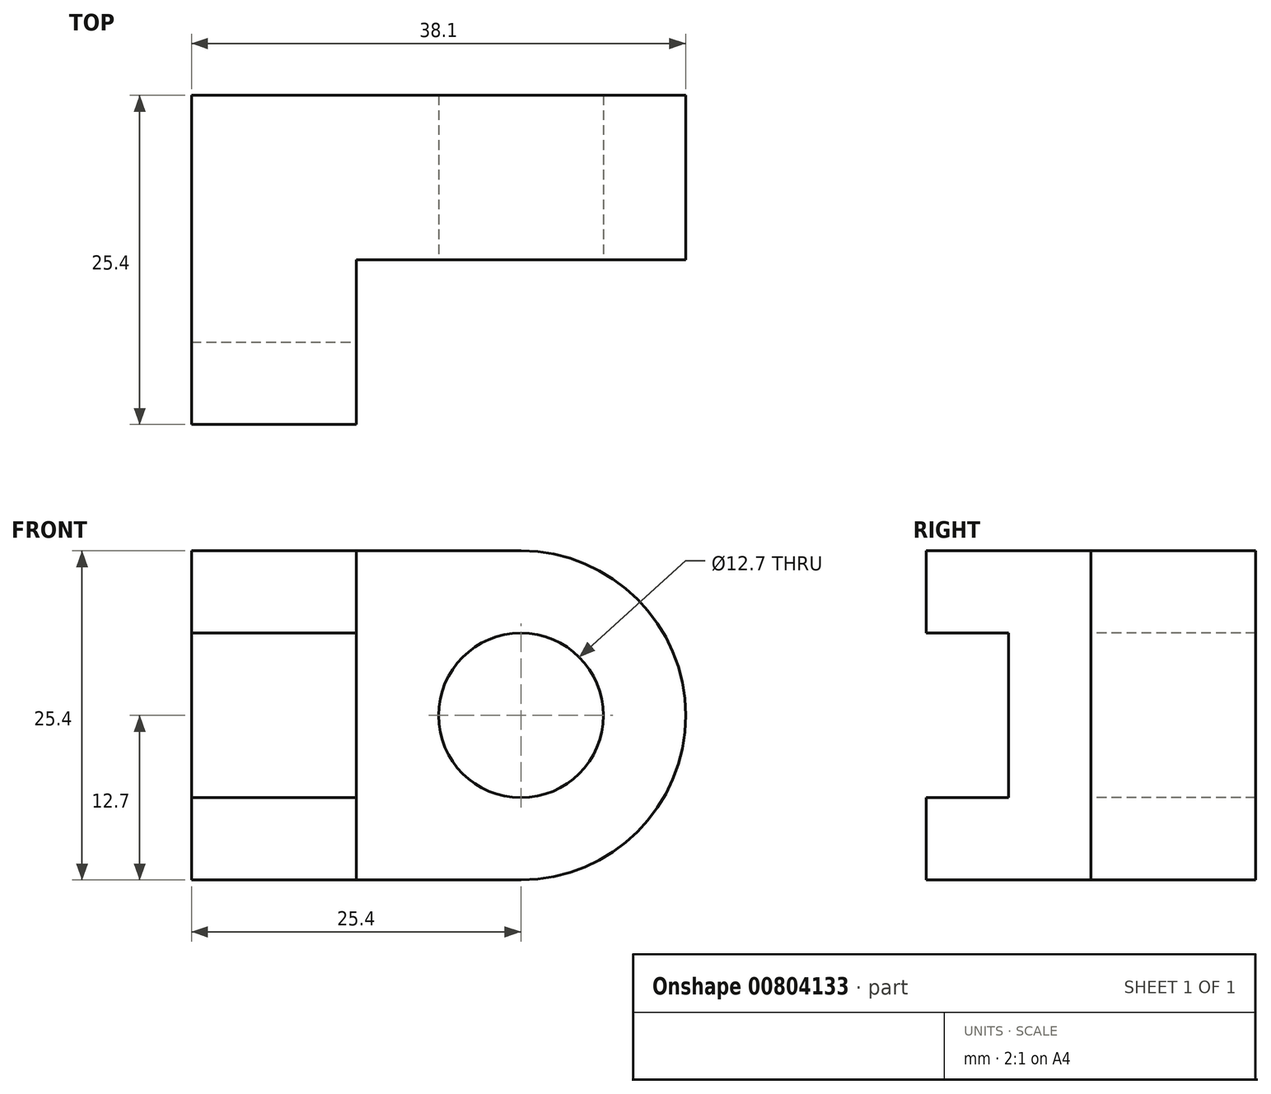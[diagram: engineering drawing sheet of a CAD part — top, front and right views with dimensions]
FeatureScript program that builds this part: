
annotation { "Feature Type Name" : "Feature", "Feature Type Description" : "" }
export const myFeature = defineFeature(function(context is Context, id is Id, definition is map)
    precondition{}
    {
        {
            var Q0;
            Q0=qCreatedBy(makeId("Front.planeOp"),FACE);
            var sketch = newSketch(context, id + "F0", { "sketchPlane" : qUnion([Q0])});
            skLineSegment(sketch, "E0", {"start": v(0, 0) * mm, "end": v(0, 25.4) * mm});
            skLineSegment(sketch, "E1", {"start": v(0, 25.4) * mm, "end": v(31.75, 25.4) * mm});
            skLineSegment(sketch, "E2", {"start": v(31.75, 25.4) * mm, "end": v(31.75, 0) * mm});
            skLineSegment(sketch, "E3", {"start": v(31.75, 0) * mm, "end": v(0, 0) * mm});
            skSolve(sketch);
        }
        {
            var Q0;
            Q0=makeQuery(id+"F0.imprint","IMPRINT",FACE,{"disambiguationData":[TD([[makeQuery(id+"F0.imprint","IMPRINT",EDGE,{"derivedFrom":sQuery(id+"F0.wireOp",EDGE,"E0")}),-1.0]])]});
            extrude(context, id + "F1", {"entities" : qUnion([Q0]), "depth" : 25.4 * mm, "offsetDistance" : 25.4 * mm});
        }
        {
            var Q0;
            Q0=makeQuery(id+"F1.opExtrude","SWEPT_FACE",FACE,{"disambiguationData":[OSD([sQuery(id+"F0.wireOp",EDGE,"E2")])]});
            var sketch = newSketch(context, id + "F2", { "sketchPlane" : qUnion([Q0])});
            skLineSegment(sketch, "E4", {"start": v(-25.4, 0) * mm, "end": v(-12.7, 0) * mm});
            skLineSegment(sketch, "E5", {"start": v(-12.7, 0) * mm, "end": v(-12.7, 25.4) * mm});
            skSolve(sketch);
        }
        {
            var Q0;
            Q0=makeQuery(id+"F2.imprint","IMPRINT",FACE,{"disambiguationData":[TD([[makeQuery(id+"F2.imprint","IMPRINT",EDGE,{"derivedFrom":sQuery(id+"F2.wireOp",EDGE,"E4")}),1.0]])]});
            extrude(context, id + "F3", {"entities" : qUnion([Q0]), "operationType" : NewBodyOperationType.REMOVE, "oppositeDirection" : true, "depth" : 19.05 * mm, "offsetDistance" : 25.4 * mm});
        }
        {
            var Q0;
            Q0=makeQuery(id+"F3.boolean.opBoolean","COPY",FACE,{"derivedFrom":makeQuery(id+"F3.opExtrude","CAP_FACE",FACE,{"disambiguationData":[OSD([sQuery(id+"F0.wireOp",EDGE,"E1"),sQuery(id+"F0.wireOp",EDGE,"E2"),sQuery(id+"F2.wireOp",EDGE,"E4"),sQuery(id+"F2.wireOp",EDGE,"E5")])],"isStart":false})});
            var sketch = newSketch(context, id + "F4", { "sketchPlane" : qUnion([Q0])});
            skLineSegment(sketch, "E6", {"start": v(-25.4, 0) * mm, "end": v(-25.4, 6.35) * mm});
            skLineSegment(sketch, "E7", {"start": v(-25.4, 6.35) * mm, "end": v(-19.05, 6.35) * mm});
            skLineSegment(sketch, "E8", {"start": v(-19.05, 6.35) * mm, "end": v(-19.05, 19.05) * mm});
            skLineSegment(sketch, "E9", {"start": v(-19.05, 19.05) * mm, "end": v(-25.4, 19.05) * mm});
            skSolve(sketch);
        }
        {
            var Q0;
            {var subQ0=sQuery(id+"F4.wireOp",EDGE,"E7");Q0=makeQuery(id+"F4.imprint","IMPRINT",FACE,{"disambiguationData":[TD([[makeQuery(id+"F4.imprint","IMPRINT",EDGE,{"derivedFrom":subQ0}),1.0]])]});}
            extrude(context, id + "F5", {"entities" : qUnion([Q0]), "operationType" : NewBodyOperationType.REMOVE, "oppositeDirection" : true, "depth" : 25.4 * mm, "offsetDistance" : 25.4 * mm});
        }
        {
            var Q0;
            Q0=makeQuery(id+"F1.opExtrude","SWEPT_FACE",FACE,{"disambiguationData":[OSD([sQuery(id+"F0.wireOp",EDGE,"E2")])]});
            extrude(context, id + "F6", {"entities" : qUnion([Q0]), "operationType" : NewBodyOperationType.ADD, "depth" : 25.4 * mm, "offsetDistance" : 25.4 * mm});
        }
        {
            var Q0;
            {var subQ0=sQuery(id+"F2.wireOp",EDGE,"E5");Q0=makeQuery(id+"F6.boolean.opBoolean","MERGE",FACE,{"derivedFrom":[makeQuery(id+"F3.boolean.opBoolean","COPY",FACE,{"derivedFrom":makeQuery(id+"F3.opExtrude","SWEPT_FACE",FACE,{"disambiguationData":[OSD([subQ0])]})}),makeQuery(id+"F6.opExtrude","SWEPT_FACE",FACE,{"disambiguationData":[OSD([subQ0])]})]});}
            var sketch = newSketch(context, id + "F7", { "sketchPlane" : qUnion([Q0])});
            skLineSegment(sketch, "E10", {"start": v(12.7, 25.4) * mm, "end": v(25.4, 25.4) * mm, "construction": true});
            skArc(sketch, "E11", {"start": v(25.4, 0) * mm, "mid": v(38.1, 12.7) * mm, "end": v(25.4, 25.4) * mm});
            skSolve(sketch);
        }
        {
            var Q0;
            {var subQ0=sQuery(id+"F7.wireOp",EDGE,"E11");Q0=makeQuery(id+"F7.imprint","IMPRINT",FACE,{"disambiguationData":[TD([[makeQuery(id+"F7.imprint","IMPRINT",EDGE,{"derivedFrom":subQ0}),-1.0]])]});}
            extrude(context, id + "F8", {"entities" : qUnion([Q0]), "operationType" : NewBodyOperationType.REMOVE, "oppositeDirection" : true, "depth" : 25.4 * mm, "offsetDistance" : 25.4 * mm});
        }
        {
            var Q0;
            {var subQ0=sQuery(id+"F2.wireOp",EDGE,"E5");Q0=makeQuery(id+"F6.boolean.opBoolean","MERGE",FACE,{"derivedFrom":[makeQuery(id+"F3.boolean.opBoolean","COPY",FACE,{"derivedFrom":makeQuery(id+"F3.opExtrude","SWEPT_FACE",FACE,{"disambiguationData":[OSD([subQ0])]})}),makeQuery(id+"F6.opExtrude","SWEPT_FACE",FACE,{"disambiguationData":[OSD([subQ0])]})]});}
            var sketch = newSketch(context, id + "F9", { "sketchPlane" : qUnion([Q0])});
            skLineSegment(sketch, "E12", {"start": v(25.4, 25.4) * mm, "end": v(25.4, 19.05) * mm, "construction": true});
            skLineSegment(sketch, "E13", {"start": v(25.4, 19.05) * mm, "end": v(25.4, 12.7) * mm, "construction": true});
            skCircle(sketch, "E14", {"center": v(25.4, 12.7) * mm, "radius": 6.35 * mm});
            skSolve(sketch);
        }
        {
            var Q0;
            Q0=makeQuery(id+"F9.imprint","IMPRINT",FACE,{"disambiguationData":[TD([[makeQuery(id+"F9.imprint","IMPRINT",EDGE,{"derivedFrom":sQuery(id+"F9.wireOp",EDGE,"E14")}),1.0]])]});
            extrude(context, id + "F10", {"entities" : qUnion([Q0]), "operationType" : NewBodyOperationType.REMOVE, "oppositeDirection" : true, "depth" : 25.4 * mm, "offsetDistance" : 25.4 * mm});
        }
    });
